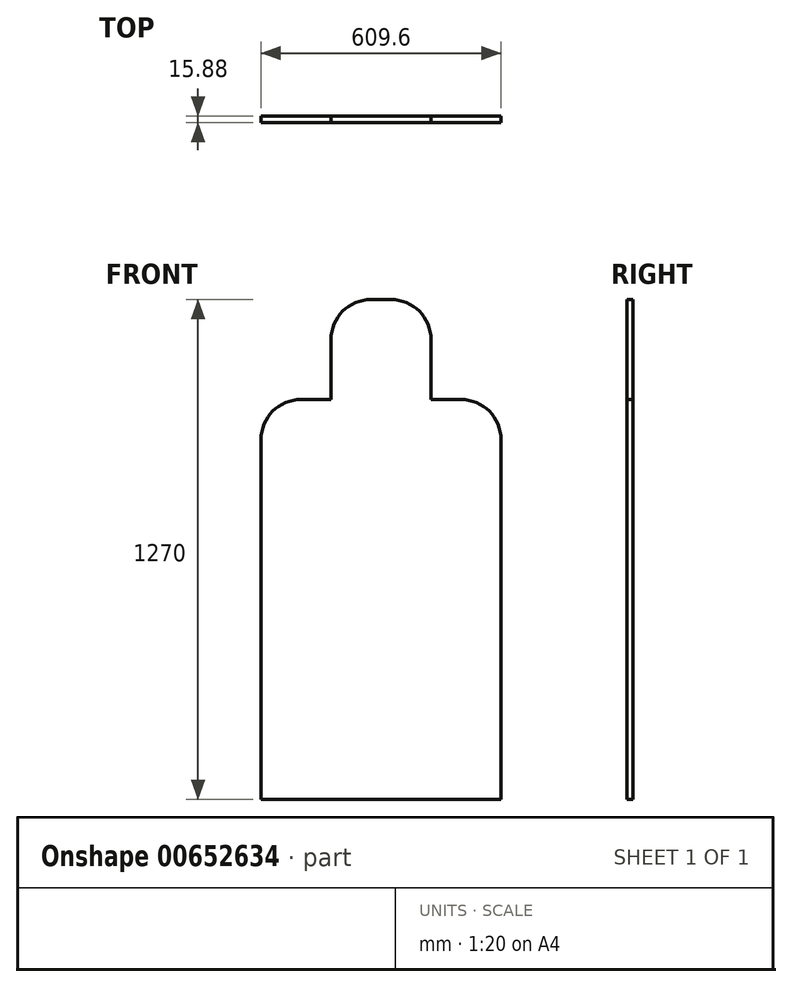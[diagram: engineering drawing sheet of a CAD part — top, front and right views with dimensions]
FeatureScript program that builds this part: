
annotation { "Feature Type Name" : "Feature", "Feature Type Description" : "" }
export const myFeature = defineFeature(function(context is Context, id is Id, definition is map)
    precondition{}
    {
        {
            var Q0;
            Q0=qCreatedBy(makeId("Front.planeOp"),FACE);
            var sketch = newSketch(context, id + "F0", { "sketchPlane" : qUnion([Q0])});
            skLineSegment(sketch, "E0.bottom", {"start": v(304.8, 508) * mm, "end": v(-304.8, 508) * mm});
            skLineSegment(sketch, "E0.top", {"start": v(304.8, -508) * mm, "end": v(-304.8, -508) * mm});
            skLineSegment(sketch, "E0.left", {"start": v(304.8, 508) * mm, "end": v(304.8, -508) * mm});
            skLineSegment(sketch, "E0.right", {"start": v(-304.8, 508) * mm, "end": v(-304.8, -508) * mm});
            skPoint(sketch, "E0.middle", {"position": v(0, 0) * mm});
            skLineSegment(sketch, "E1", {"start": v(-127, 508) * mm, "end": v(-127, 762) * mm});
            skLineSegment(sketch, "E2", {"start": v(-127, 762) * mm, "end": v(127, 762) * mm});
            skLineSegment(sketch, "E3", {"start": v(127, 762) * mm, "end": v(127, 508) * mm});
            skSolve(sketch);
        }
        {
            var Q0;
            Q0=makeQuery(id+"F0.imprint","IMPRINT",FACE,{"disambiguationData":[TD([[makeQuery(id+"F0.imprint","IMPRINT",EDGE,{"derivedFrom":sQuery(id+"F0.wireOp",EDGE,"E0.top")}),-1.0]])]});
            var Q1;
            {var subQ0=sQuery(id+"F0.wireOp",EDGE,"E1");Q1=makeQuery(id+"F0.imprint","IMPRINT",FACE,{"disambiguationData":[TD([[makeQuery(id+"F0.imprint","IMPRINT",EDGE,{"derivedFrom":subQ0}),-1.0]])]});}
            extrude(context, id + "F1", {"entities" : qUnion([Q0, Q1]), "depth" : 15.88 * mm, "offsetDistance" : 25.4 * mm});
        }
        {
            var Q0;
            Q0=makeQuery(id+"F1.opExtrude","SWEPT_EDGE",EDGE,{"disambiguationData":[OSD([sQuery(id+"F0.wireOp",EDGE,"E2"),sQuery(id+"F0.wireOp",EDGE,"E3")])]});
            var Q1;
            Q1=makeQuery(id+"F1.opExtrude","SWEPT_EDGE",EDGE,{"disambiguationData":[OSD([sQuery(id+"F0.wireOp",EDGE,"E0.bottom"),sQuery(id+"F0.wireOp",EDGE,"E0.left")])]});
            var Q2;
            Q2=makeQuery(id+"F1.opExtrude","SWEPT_EDGE",EDGE,{"disambiguationData":[OSD([sQuery(id+"F0.wireOp",EDGE,"E0.bottom"),sQuery(id+"F0.wireOp",EDGE,"E0.right")])]});
            var Q3;
            Q3=makeQuery(id+"F1.opExtrude","SWEPT_EDGE",EDGE,{"disambiguationData":[OSD([sQuery(id+"F0.wireOp",EDGE,"E1"),sQuery(id+"F0.wireOp",EDGE,"E2")])]});
            fillet(context, id + "F2", {"entities" : qUnion([Q0, Q1, Q2, Q3]), "radius" : 101.6 * mm, "tangentPropagation" : true, "allowEdgeOverflow" : false});
        }
    });
